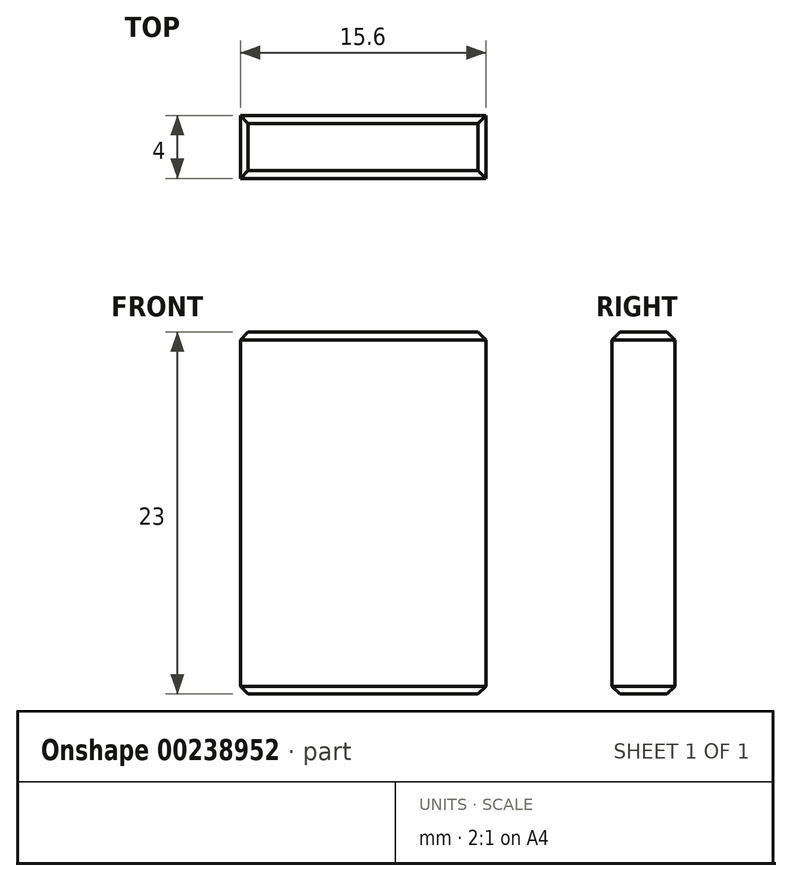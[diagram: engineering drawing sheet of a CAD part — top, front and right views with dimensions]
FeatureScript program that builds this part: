
annotation { "Feature Type Name" : "Feature", "Feature Type Description" : "" }
export const myFeature = defineFeature(function(context is Context, id is Id, definition is map)
    precondition{}
    {
        {
            var Q0;
            Q0=qCreatedBy(makeId("Front.planeOp"),FACE);
            var sketch = newSketch(context, id + "F0", { "sketchPlane" : qUnion([Q0])});
            skLineSegment(sketch, "E0", {"start": v(-7.8, 11.5) * mm, "end": v(-7.8, 0) * mm});
            skLineSegment(sketch, "E1", {"start": v(-7.8, 11.5) * mm, "end": v(0, 11.5) * mm});
            skLineSegment(sketch, "E2.MirrorCS", {"start": v(7.8, 11.5) * mm, "end": v(0, 11.5) * mm});
            skLineSegment(sketch, "E3.MirrorCS", {"start": v(7.8, 11.5) * mm, "end": v(7.8, 0) * mm});
            skLineSegment(sketch, "E4.MirrorCS", {"start": v(7.8, -11.5) * mm, "end": v(7.8, 0) * mm});
            skLineSegment(sketch, "E5.MirrorCS", {"start": v(7.8, -11.5) * mm, "end": v(0, -11.5) * mm});
            skLineSegment(sketch, "E6.MirrorCS", {"start": v(-7.8, -11.5) * mm, "end": v(0, -11.5) * mm});
            skLineSegment(sketch, "E7.MirrorCS", {"start": v(-7.8, -11.5) * mm, "end": v(-7.8, 0) * mm});
            skSolve(sketch);
        }
        {
            var Q0;
            Q0 = qSketchRegion(id + "F0", true);
            extrude(context, id + "F1", {"entities" : qUnion([Q0]), "oppositeDirection" : true, "depth" : 4 * mm});
        }
        {
            var Q0;
            Q0=makeQuery(id+"F1.opExtrude","SWEPT_EDGE",EDGE,{"disambiguationData":[OSD([sQuery(id+"F0.wireOp",EDGE,"E0"),sQuery(id+"F0.wireOp",EDGE,"E1")])]});
            var Q1;
            Q1=makeQuery(id+"F1.opExtrude","CAP_EDGE",EDGE,{"disambiguationData":[OSD([sQuery(id+"F0.wireOp",EDGE,"E1"),sQuery(id+"F0.wireOp",EDGE,"E2.MirrorCS")])],"isStart":true});
            var Q2;
            Q2=makeQuery(id+"F1.opExtrude","SWEPT_EDGE",EDGE,{"disambiguationData":[OSD([sQuery(id+"F0.wireOp",EDGE,"E2.MirrorCS"),sQuery(id+"F0.wireOp",EDGE,"E3.MirrorCS")])]});
            var Q3;
            Q3=makeQuery(id+"F1.opExtrude","SWEPT_FACE",FACE,{"disambiguationData":[OSD([sQuery(id+"F0.wireOp",EDGE,"E1"),sQuery(id+"F0.wireOp",EDGE,"E2.MirrorCS")])]});
            var Q4;
            Q4=makeQuery(id+"F1.opExtrude","CAP_EDGE",EDGE,{"disambiguationData":[OSD([sQuery(id+"F0.wireOp",EDGE,"E5.MirrorCS"),sQuery(id+"F0.wireOp",EDGE,"E6.MirrorCS")])],"isStart":true});
            var Q5;
            Q5=makeQuery(id+"F1.opExtrude","SWEPT_EDGE",EDGE,{"disambiguationData":[OSD([sQuery(id+"F0.wireOp",EDGE,"E6.MirrorCS"),sQuery(id+"F0.wireOp",EDGE,"E7.MirrorCS")])]});
            var Q6;
            Q6=makeQuery(id+"F1.opExtrude","SWEPT_EDGE",EDGE,{"disambiguationData":[OSD([sQuery(id+"F0.wireOp",EDGE,"E4.MirrorCS"),sQuery(id+"F0.wireOp",EDGE,"E5.MirrorCS")])]});
            var Q7;
            Q7=makeQuery(id+"F1.opExtrude","CAP_EDGE",EDGE,{"disambiguationData":[OSD([sQuery(id+"F0.wireOp",EDGE,"E5.MirrorCS"),sQuery(id+"F0.wireOp",EDGE,"E6.MirrorCS")])],"isStart":false});
            chamfer(context, id + "F2", {"entities" : qUnion([Q0, Q1, Q2, Q3, Q4, Q5, Q6, Q7]), "width" : 0.5 * mm, "tangentPropagation" : true});
        }
    });
